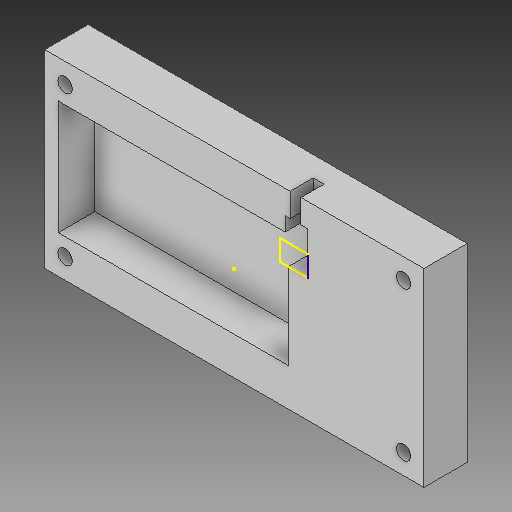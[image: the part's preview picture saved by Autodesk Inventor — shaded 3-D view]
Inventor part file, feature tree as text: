
AUTODESK INVENTOR PART (.ipt)
format: ipt  version: 2018 (Build 220112000, 112)  size: 288,256 bytes
history: native  units: in
note: dims shown in document units (in); Inventor stores cm internally (conversion verified against a paired STEP export)
features: extrude x11, sketch x8, projected_geometry x5, plane x4, hole x2
ambient origin geometry x8: Origin, YZ Plane, XZ Plane, XY Plane, X Axis, Y Axis, Z Axis, Center Point
bodies: Solid1 (feature_tree)
feature tree (30):
  extrude  "Extrusion1"  Depth=3.5in
  extrude  "Extrusion2"  Depth=2.105in
  extrude  "Extrusion4"  Depth=0.25in
  plane  "Work Plane1"
  plane  "Work Plane2"
  extrude  "Extrusion5"  Depth=0.38in
  plane  "Work Plane3"
  plane  "Work Plane4"
  sketch  "Sketch6"  dims[d4=0.25in d5=4.075in]
  extrude  "Extrusion6"  Depth=0.675in
  extrude  "Extrusion7"  Depth=0.2in
  extrude  "Extrusion8"  Depth=0.125in TaperAngle=0.0deg
  extrude  "Extrusion9"  Depth=0.25in
  extrude  "Extrusion10"  Depth=0.25in
  hole  "Hole2"  [1 undecoded]
  extrude  "Extrusion11"  Depth=0.25in
  extrude  "Extrusion12"  Depth=0.25in
  sketch  "Sketch3"  dims[d0=7.0in d1=3.5in]
  projected_geometry  "Projected Loop2"
  sketch  "Sketch5"  dims[d2=4.25in d3=2.105in]
  projected_geometry  "Projected Loop3"
  sketch  "Sketch7"  dims[d7=0.33in d8=0.38in]
  projected_geometry  "Projected Loop4"
  sketch  "Sketch8"  dims[d9=0.675in d10=0.0in d13=0.525in]
  sketch  "Sketch9"  dims[d15=0.2in d17=0.4in]
  hole  "Hole1"  [1 undecoded]
  sketch  "Sketch10"  dims[d18=0.5in d19=0.0in d22=0.125in d23=0.0in]
  projected_geometry  "Projected Loop5"
  sketch  "Sketch12"  dims[d24=0.0625in d25=0.22in d26=1.45in d27=2.0in d28=0.75in d29=0.25in d30=0.125in d31=0.0in d32=0.5in d33=0.125in d34=0.125in d35=0.875in d36=0.375in d37=0.0in d38=0.375in d39=0.0in d40=0.25in d41=0.0in d42=0.25in d43=0.0in d44=0.25in d45=0.0in d46=0.266in d47=0.75in d48=0.375in d49=0.25in d50=0.5635in d51=1.0in d52=0.0in d53=0.25in d54=0.0in d55=1.0in d56=0.0in]
  projected_geometry  "Projected Loop13"
note: 2 required parameter values undecoded (feature->parameter linkage not recoverable at this tier; creation-order binding heuristic only, values carry confidence <= 0.55)
